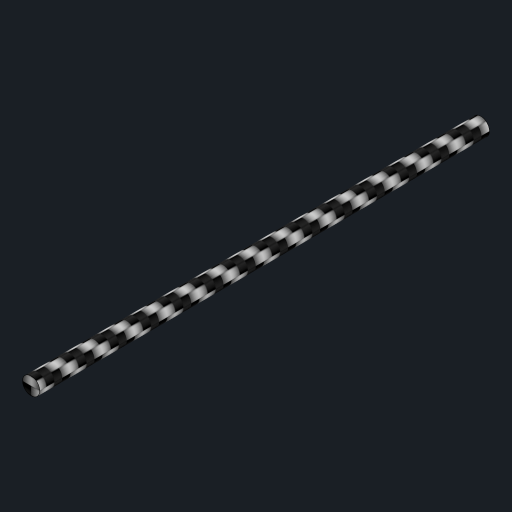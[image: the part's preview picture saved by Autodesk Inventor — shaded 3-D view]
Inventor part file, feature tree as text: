
AUTODESK INVENTOR PART (.ipt)
format: ipt  version: 2023 (Build 270158000, 158)  size: 103,936 bytes
history: native  units: in
note: dims shown in document units (in); Inventor stores cm internally (conversion verified against a paired STEP export)
features: other x1, extrude x1, sketch x1
ambient origin geometry x8: Origin, YZ Plane, XZ Plane, XY Plane, X Axis, Y Axis, Z Axis, Center Point
bodies: Body1 (feature_tree)
feature tree (3):
  other  "ソリッド1"
  extrude  "押し出し1"  Depth=0.0787in
  sketch  "スケッチ1"
